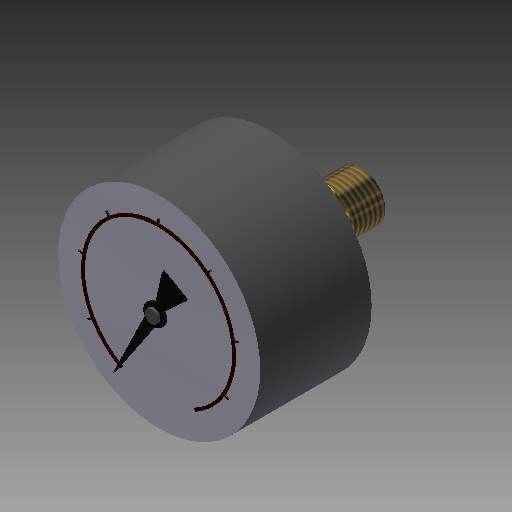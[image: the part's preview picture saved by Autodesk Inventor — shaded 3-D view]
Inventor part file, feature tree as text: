
AUTODESK INVENTOR PART (.ipt)
format: ipt  version: 2018 (Build 220112000, 112)  size: 186,880 bytes
history: native  units: mm
features: imported_body x1, thread x1
ambient origin geometry x8: Origin, YZ Plane, XZ Plane, XY Plane, X Axis, Y Axis, Z Axis, Center Point
bodies: Solid1 (feature_tree)
feature tree (2):
  imported_body  "Base1"
  thread  "Thread1"  [1 undecoded]
note: 1 required parameter value undecoded (feature->parameter linkage not recoverable at this tier; creation-order binding heuristic only, values carry confidence <= 0.55)
